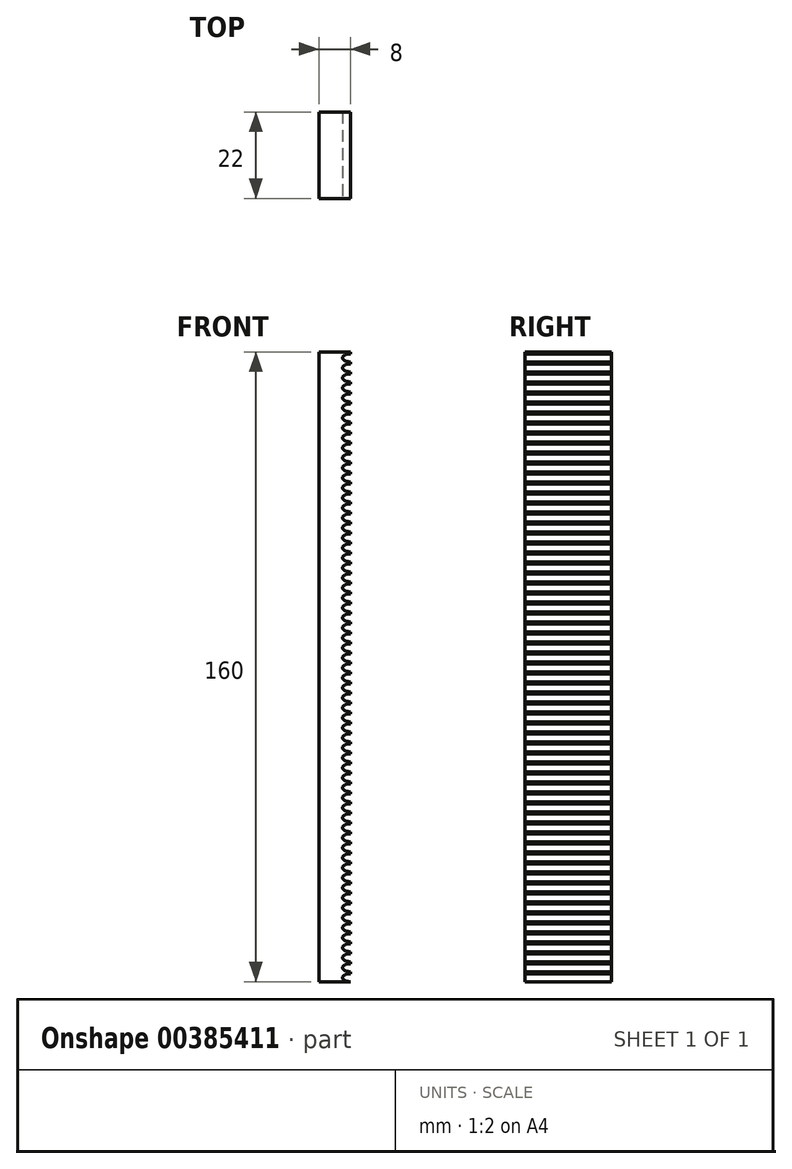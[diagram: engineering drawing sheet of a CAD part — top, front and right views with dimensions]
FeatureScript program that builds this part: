
annotation { "Feature Type Name" : "Feature", "Feature Type Description" : "" }
export const myFeature = defineFeature(function(context is Context, id is Id, definition is map)
    precondition{}
    {
        {
            var Q0;
            Q0=qCreatedBy(makeId("Front.planeOp"),FACE);
            var sketch = newSketch(context, id + "F0", { "sketchPlane" : qUnion([Q0])});
            skLineSegment(sketch, "E0", {"start": v(-30.32, 103.09) * mm, "end": v(-30.32, -56.91) * mm});
            skLineSegment(sketch, "E1", {"start": v(-30.32, -56.91) * mm, "end": v(-22.32, -56.91) * mm});
            skLineSegment(sketch, "E2", {"start": v(-22.32, -56.91) * mm, "end": v(-22.32, 103.09) * mm});
            skLineSegment(sketch, "E3", {"start": v(-22.32, 103.09) * mm, "end": v(-30.32, 103.09) * mm});
            skEllipticalArc(sketch, "E4", {});
            skEllipticalArc(sketch, "E5.0.1.0", {});
            skEllipticalArc(sketch, "E5.0.2.0", {});
            skEllipticalArc(sketch, "E5.0.3.0", {});
            skEllipticalArc(sketch, "E5.0.4.0", {});
            skEllipticalArc(sketch, "E5.0.5.0", {});
            skEllipticalArc(sketch, "E5.0.6.0", {});
            skEllipticalArc(sketch, "E5.0.7.0", {});
            skEllipticalArc(sketch, "E5.0.8.0", {});
            skEllipticalArc(sketch, "E5.0.9.0", {});
            skEllipticalArc(sketch, "E5.0.10.0", {});
            skEllipticalArc(sketch, "E5.0.11.0", {});
            skEllipticalArc(sketch, "E5.0.12.0", {});
            skEllipticalArc(sketch, "E5.0.13.0", {});
            skEllipticalArc(sketch, "E5.0.14.0", {});
            skEllipticalArc(sketch, "E5.0.15.0", {});
            skEllipticalArc(sketch, "E5.0.16.0", {});
            skEllipticalArc(sketch, "E5.0.17.0", {});
            skEllipticalArc(sketch, "E5.0.18.0", {});
            skEllipticalArc(sketch, "E5.0.19.0", {});
            skEllipticalArc(sketch, "E5.0.20.0", {});
            skEllipticalArc(sketch, "E5.0.21.0", {});
            skEllipticalArc(sketch, "E5.0.22.0", {});
            skEllipticalArc(sketch, "E5.0.23.0", {});
            skEllipticalArc(sketch, "E5.0.24.0", {});
            skEllipticalArc(sketch, "E5.0.25.0", {});
            skEllipticalArc(sketch, "E5.0.26.0", {});
            skEllipticalArc(sketch, "E5.0.27.0", {});
            skEllipticalArc(sketch, "E5.0.28.0", {});
            skEllipticalArc(sketch, "E5.0.29.0", {});
            skEllipticalArc(sketch, "E5.0.30.0", {});
            skEllipticalArc(sketch, "E5.0.31.0", {});
            skEllipticalArc(sketch, "E5.0.32.0", {});
            skEllipticalArc(sketch, "E5.0.33.0", {});
            skEllipticalArc(sketch, "E5.0.34.0", {});
            skEllipticalArc(sketch, "E5.0.35.0", {});
            skEllipticalArc(sketch, "E5.0.36.0", {});
            skEllipticalArc(sketch, "E5.0.37.0", {});
            skEllipticalArc(sketch, "E5.0.38.0", {});
            skEllipticalArc(sketch, "E5.0.39.0", {});
            skEllipticalArc(sketch, "E5.0.40.0", {});
            skEllipticalArc(sketch, "E5.0.41.0", {});
            skEllipticalArc(sketch, "E5.0.42.0", {});
            skEllipticalArc(sketch, "E5.0.43.0", {});
            skEllipticalArc(sketch, "E5.0.44.0", {});
            skEllipticalArc(sketch, "E5.0.45.0", {});
            skEllipticalArc(sketch, "E5.0.46.0", {});
            skEllipticalArc(sketch, "E5.0.47.0", {});
            skEllipticalArc(sketch, "E5.0.48.0", {});
            skEllipticalArc(sketch, "E5.0.49.0", {});
            skEllipticalArc(sketch, "E5.0.50.0", {});
            skEllipticalArc(sketch, "E5.0.51.0", {});
            skEllipticalArc(sketch, "E5.0.52.0", {});
            skEllipticalArc(sketch, "E5.0.53.0", {});
            skEllipticalArc(sketch, "E5.0.54.0", {});
            skEllipticalArc(sketch, "E5.0.55.0", {});
            skEllipticalArc(sketch, "E5.0.56.0", {});
            skEllipticalArc(sketch, "E5.0.57.0", {});
            skEllipticalArc(sketch, "E5.0.58.0", {});
            skEllipticalArc(sketch, "E5.0.59.0", {});
            skEllipticalArc(sketch, "E5.0.60.0", {});
            skEllipticalArc(sketch, "E5.0.61.0", {});
            skEllipticalArc(sketch, "E5.0.62.0", {});
            skLineSegment(sketch, "E5.direction1", {"start": v(-22.32, -56.91) * mm, "end": v(3.08, -56.91) * mm, "construction": true});
            skLineSegment(sketch, "E5.direction2", {"start": v(-22.32, -56.91) * mm, "end": v(-22.32, -54.37) * mm, "construction": true});
            const initialGuessF0  = {"E4": [-0.022320480465888963, -0.05589835933113098, 1, 0, 0.0019939000000000003, 0.001016, 1.5707963267948966, 4.71238898038469], "E5.0.1.0": [-0.022320480465888963, -0.05335835929328203, 1, 0, 0.0019939000000000003, 0.001016, 1.5707963267948966, 4.71238898038469], "E5.0.2.0": [-0.022320480465888963, -0.050818359255433085, 1, 0, 0.0019939000000000003, 0.001016, 1.5707963267948966, 4.71238898038469], "E5.0.3.0": [-0.022320480465888963, -0.04827835921758414, 1, 0, 0.0019939000000000003, 0.001016, 1.5707963267948966, 4.71238898038469], "E5.0.4.0": [-0.022320480465888963, -0.04573835917973519, 1, 0, 0.0019939000000000003, 0.001016, 1.5707963267948966, 4.71238898038469], "E5.0.5.0": [-0.022320480465888963, -0.043198359141886244, 1, 0, 0.0019939000000000003, 0.001016, 1.5707963267948966, 4.71238898038469], "E5.0.6.0": [-0.022320480465888963, -0.0406583591040373, 1, 0, 0.0019939000000000003, 0.001016, 1.5707963267948966, 4.71238898038469], "E5.0.7.0": [-0.022320480465888963, -0.03811835906618835, 1, 0, 0.0019939000000000003, 0.001016, 1.5707963267948966, 4.71238898038469], "E5.0.8.0": [-0.022320480465888963, -0.035578359028339404, 1, 0, 0.0019939000000000003, 0.001016, 1.5707963267948966, 4.71238898038469], "E5.0.9.0": [-0.022320480465888963, -0.03303835899049046, 1, 0, 0.0019939000000000003, 0.001016, 1.5707963267948966, 4.71238898038469], "E5.0.10.0": [-0.022320480465888963, -0.03049835895264151, 1, 0, 0.0019939000000000003, 0.001016, 1.5707963267948966, 4.71238898038469], "E5.0.11.0": [-0.022320480465888963, -0.027958358914792564, 1, 0, 0.0019939000000000003, 0.001016, 1.5707963267948966, 4.71238898038469], "E5.0.12.0": [-0.022320480465888963, -0.025418358876943617, 1, 0, 0.0019939000000000003, 0.001016, 1.5707963267948966, 4.71238898038469], "E5.0.13.0": [-0.022320480465888963, -0.02287835883909467, 1, 0, 0.0019939000000000003, 0.001016, 1.5707963267948966, 4.71238898038469], "E5.0.14.0": [-0.022320480465888963, -0.020338358801245723, 1, 0, 0.0019939000000000003, 0.001016, 1.5707963267948966, 4.71238898038469], "E5.0.15.0": [-0.022320480465888963, -0.017798358763396777, 1, 0, 0.0019939000000000003, 0.001016, 1.5707963267948966, 4.71238898038469], "E5.0.16.0": [-0.022320480465888963, -0.01525835872554783, 1, 0, 0.0019939000000000003, 0.001016, 1.5707963267948966, 4.71238898038469], "E5.0.17.0": [-0.022320480465888963, -0.012718358687698883, 1, 0, 0.0019939000000000003, 0.001016, 1.5707963267948966, 4.71238898038469], "E5.0.18.0": [-0.022320480465888963, -0.010178358649849936, 1, 0, 0.0019939000000000003, 0.001016, 1.5707963267948966, 4.71238898038469], "E5.0.19.0": [-0.022320480465888963, -0.007638358612000989, 1, 0, 0.0019939000000000003, 0.001016, 1.5707963267948966, 4.71238898038469], "E5.0.20.0": [-0.022320480465888963, -0.005098358574152043, 1, 0, 0.0019939000000000003, 0.001016, 1.5707963267948966, 4.71238898038469], "E5.0.21.0": [-0.022320480465888963, -0.002558358536303096, 1, 0, 0.0019939000000000003, 0.001016, 1.5707963267948966, 4.71238898038469], "E5.0.22.0": [-0.022320480465888963, -1.8358498454149053e-05, 1, 0, 0.0019939000000000003, 0.001016, 1.5707963267948966, 4.71238898038469], "E5.0.23.0": [-0.022320480465888963, 0.0025216415393947977, 1, 0, 0.0019939000000000003, 0.001016, 1.5707963267948966, 4.71238898038469], "E5.0.24.0": [-0.022320480465888963, 0.0050616415772437445, 1, 0, 0.0019939000000000003, 0.001016, 1.5707963267948966, 4.71238898038469], "E5.0.25.0": [-0.022320480465888963, 0.007601641615092691, 1, 0, 0.0019939000000000003, 0.001016, 1.5707963267948966, 4.71238898038469], "E5.0.26.0": [-0.022320480465888963, 0.010141641652941638, 1, 0, 0.0019939000000000003, 0.001016, 1.5707963267948966, 4.71238898038469], "E5.0.27.0": [-0.022320480465888963, 0.012681641690790585, 1, 0, 0.0019939000000000003, 0.001016, 1.5707963267948966, 4.71238898038469], "E5.0.28.0": [-0.022320480465888963, 0.015221641728639532, 1, 0, 0.0019939000000000003, 0.001016, 1.5707963267948966, 4.71238898038469], "E5.0.29.0": [-0.022320480465888963, 0.01776164176648848, 1, 0, 0.0019939000000000003, 0.001016, 1.5707963267948966, 4.71238898038469], "E5.0.30.0": [-0.022320480465888963, 0.020301641804337425, 1, 0, 0.0019939000000000003, 0.001016, 1.5707963267948966, 4.71238898038469], "E5.0.31.0": [-0.022320480465888963, 0.022841641842186372, 1, 0, 0.0019939000000000003, 0.001016, 1.5707963267948966, 4.71238898038469], "E5.0.32.0": [-0.022320480465888963, 0.02538164188003532, 1, 0, 0.0019939000000000003, 0.001016, 1.5707963267948966, 4.71238898038469], "E5.0.33.0": [-0.022320480465888963, 0.027921641917884266, 1, 0, 0.0019939000000000003, 0.001016, 1.5707963267948966, 4.71238898038469], "E5.0.34.0": [-0.022320480465888963, 0.030461641955733212, 1, 0, 0.0019939000000000003, 0.001016, 1.5707963267948966, 4.71238898038469], "E5.0.35.0": [-0.022320480465888963, 0.03300164199358216, 1, 0, 0.0019939000000000003, 0.001016, 1.5707963267948966, 4.71238898038469], "E5.0.36.0": [-0.022320480465888963, 0.035541642031431106, 1, 0, 0.0019939000000000003, 0.001016, 1.5707963267948966, 4.71238898038469], "E5.0.37.0": [-0.022320480465888963, 0.03808164206928005, 1, 0, 0.0019939000000000003, 0.001016, 1.5707963267948966, 4.71238898038469], "E5.0.38.0": [-0.022320480465888963, 0.040621642107129, 1, 0, 0.0019939000000000003, 0.001016, 1.5707963267948966, 4.71238898038469], "E5.0.39.0": [-0.022320480465888963, 0.043161642144977946, 1, 0, 0.0019939000000000003, 0.001016, 1.5707963267948966, 4.71238898038469], "E5.0.40.0": [-0.022320480465888963, 0.04570164218282689, 1, 0, 0.0019939000000000003, 0.001016, 1.5707963267948966, 4.71238898038469], "E5.0.41.0": [-0.022320480465888963, 0.04824164222067584, 1, 0, 0.0019939000000000003, 0.001016, 1.5707963267948966, 4.71238898038469], "E5.0.42.0": [-0.022320480465888963, 0.05078164225852479, 1, 0, 0.0019939000000000003, 0.001016, 1.5707963267948966, 4.71238898038469], "E5.0.43.0": [-0.022320480465888963, 0.053321642296373734, 1, 0, 0.0019939000000000003, 0.001016, 1.5707963267948966, 4.71238898038469], "E5.0.44.0": [-0.022320480465888963, 0.05586164233422268, 1, 0, 0.0019939000000000003, 0.001016, 1.5707963267948966, 4.71238898038469], "E5.0.45.0": [-0.022320480465888963, 0.05840164237207163, 1, 0, 0.0019939000000000003, 0.001016, 1.5707963267948966, 4.71238898038469], "E5.0.46.0": [-0.022320480465888963, 0.060941642409920574, 1, 0, 0.0019939000000000003, 0.001016, 1.5707963267948966, 4.71238898038469], "E5.0.47.0": [-0.022320480465888963, 0.06348164244776952, 1, 0, 0.0019939000000000003, 0.001016, 1.5707963267948966, 4.71238898038469], "E5.0.48.0": [-0.022320480465888963, 0.06602164248561847, 1, 0, 0.0019939000000000003, 0.001016, 1.5707963267948966, 4.71238898038469], "E5.0.49.0": [-0.022320480465888963, 0.06856164252346741, 1, 0, 0.0019939000000000003, 0.001016, 1.5707963267948966, 4.71238898038469], "E5.0.50.0": [-0.022320480465888963, 0.07110164256131636, 1, 0, 0.0019939000000000003, 0.001016, 1.5707963267948966, 4.71238898038469], "E5.0.51.0": [-0.022320480465888963, 0.07364164259916532, 1, 0, 0.0019939000000000003, 0.001016, 1.5707963267948966, 4.71238898038469], "E5.0.52.0": [-0.022320480465888963, 0.07618164263701425, 1, 0, 0.0019939000000000003, 0.001016, 1.5707963267948966, 4.71238898038469], "E5.0.53.0": [-0.022320480465888963, 0.07872164267486319, 1, 0, 0.0019939000000000003, 0.001016, 1.5707963267948966, 4.71238898038469], "E5.0.54.0": [-0.022320480465888963, 0.08126164271271215, 1, 0, 0.0019939000000000003, 0.001016, 1.5707963267948966, 4.71238898038469], "E5.0.55.0": [-0.022320480465888963, 0.08380164275056111, 1, 0, 0.0019939000000000003, 0.001016, 1.5707963267948966, 4.71238898038469], "E5.0.56.0": [-0.022320480465888963, 0.08634164278841004, 1, 0, 0.0019939000000000003, 0.001016, 1.5707963267948966, 4.71238898038469], "E5.0.57.0": [-0.022320480465888963, 0.08888164282625897, 1, 0, 0.0019939000000000003, 0.001016, 1.5707963267948966, 4.71238898038469], "E5.0.58.0": [-0.022320480465888963, 0.09142164286410794, 1, 0, 0.0019939000000000003, 0.001016, 1.5707963267948966, 4.71238898038469], "E5.0.59.0": [-0.022320480465888963, 0.0939616429019569, 1, 0, 0.0019939000000000003, 0.001016, 1.5707963267948966, 4.71238898038469], "E5.0.60.0": [-0.022320480465888963, 0.09650164293980583, 1, 0, 0.0019939000000000003, 0.001016, 1.5707963267948966, 4.71238898038469], "E5.0.61.0": [-0.022320480465888963, 0.09904164297765476, 1, 0, 0.0019939000000000003, 0.001016, 1.5707963267948966, 4.71238898038469], "E5.0.62.0": [-0.022320480465888963, 0.10158164301550372, 1, 0, 0.0019939000000000003, 0.001016, 1.5707963267948966, 4.71238898038469]};
            skSetInitialGuess(sketch, initialGuessF0);
            skSolve(sketch);
        }
        {
            var Q0;
            Q0=makeQuery(id+"F0.imprint","IMPRINT",FACE,{"disambiguationData":[TD([[makeQuery(id+"F0.imprint","IMPRINT",EDGE,{"derivedFrom":sQuery(id+"F0.wireOp",EDGE,"E0")}),1.0]])]});
            extrude(context, id + "F1", {"entities" : qUnion([Q0]), "depth" : 22 * mm});
        }
    });
